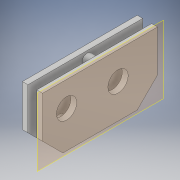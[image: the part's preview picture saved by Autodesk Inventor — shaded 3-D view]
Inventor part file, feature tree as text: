
AUTODESK INVENTOR PART (.ipt)
format: ipt  version: 2017 (Build 210142000, 142)  size: 157,696 bytes
history: native  units: in
note: dims shown in document units (in); Inventor stores cm internally (conversion verified against a paired STEP export)
features: extrude x5, sketch x5, chamfer x2, hole x2, plane x1, thicken_offset x1
ambient origin geometry x8: Origin, YZ Plane, XZ Plane, XY Plane, X Axis, Y Axis, Z Axis, Center Point
bodies: Solid1 (feature_tree)
feature tree (16):
  extrude  "Extrusion1"  Depth=0.125in TaperAngle=45.0deg
  chamfer  "Chamfer1"  Distance=0.125in Angle=45.0deg
  chamfer  "Chamfer2"  Distance=1.0in
  hole  "Hole1"  [1 undecoded]
  hole  "Hole2"  [1 undecoded]
  extrude  "Extrusion2"  Depth=0.125in TaperAngle=0.0deg
  plane  "Work Plane1"
  extrude  "Extrusion3"  Depth=0.125in
  extrude  "Extrusion4"  Depth=0.125in
  thicken_offset  "Thicken1"
  extrude  "Extrusion5"  Depth=0.125in TaperAngle=0.0deg
  sketch  "Sketch1"  dims[d0=0.125in d1=0.0in d2=0.125in d3=0.125in d4=45.0deg d5=0.125in d6=0.125in d7=45.0deg d8=1.0in d9=1.0in]
  sketch  "Sketch2"  dims[d10=0.125in d11=0.75in d12=0.375in d13=0.25in d14=0.5635in d15=0.125in d16=0.8108in d17=1.0in d18=1.0in]
  sketch  "Sketch3"  dims[d19=0.125in d20=0.75in d21=0.375in d22=0.25in d23=0.5635in d24=0.125in d25=0.8108in d26=10.0in d27=0.0in]
  sketch  "Sketch4"  dims[d28=0.001in d29=0.125in d30=0.0in]
  sketch  "Sketch5"  dims[d31=0.125in d32=0.0in d33=0.001in d34=0.001in d35=0.125in d36=0.0in]
note: 2 required parameter values undecoded (feature->parameter linkage not recoverable at this tier; creation-order binding heuristic only, values carry confidence <= 0.55)
